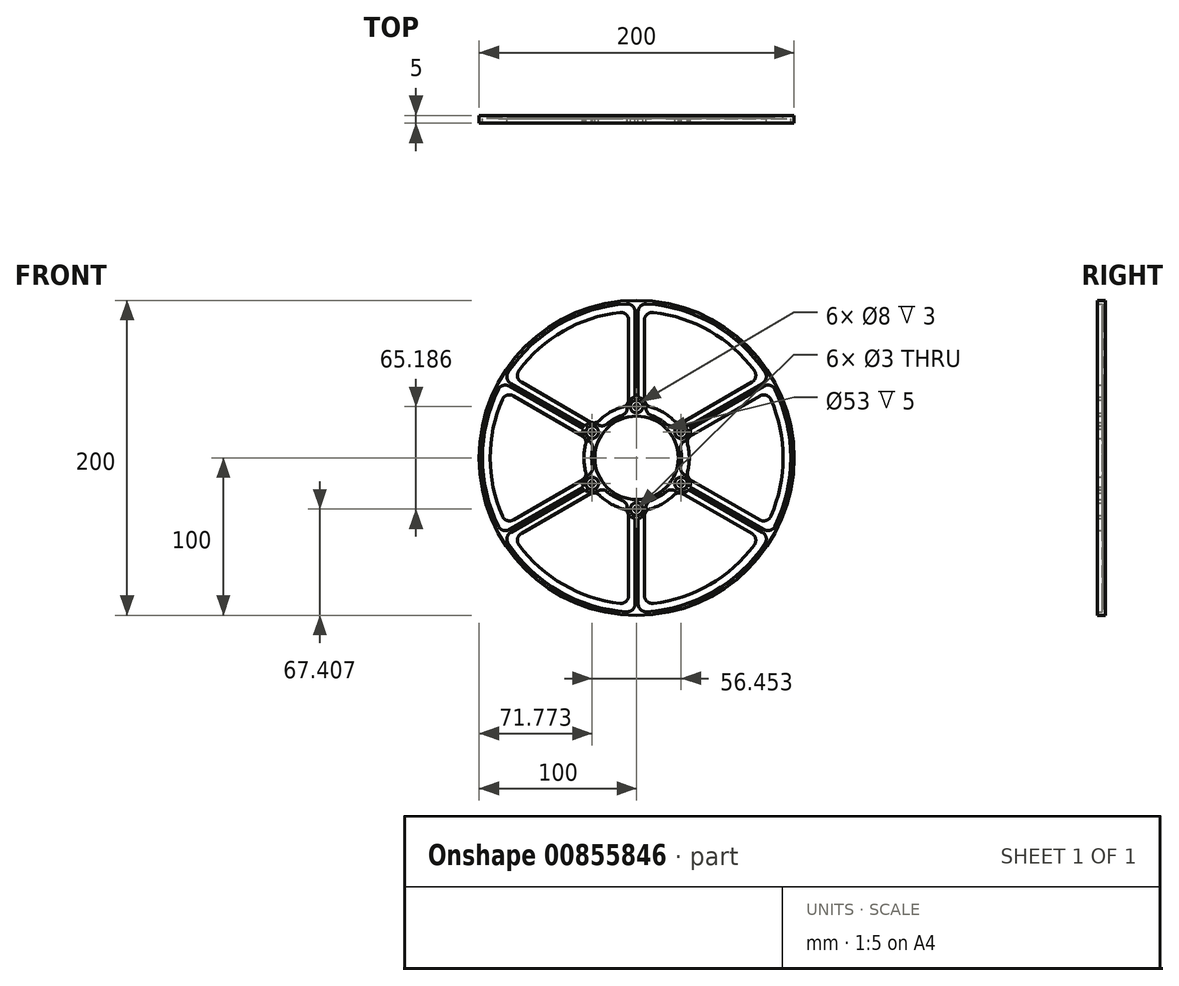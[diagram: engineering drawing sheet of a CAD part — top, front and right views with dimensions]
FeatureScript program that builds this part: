
annotation { "Feature Type Name" : "Feature", "Feature Type Description" : "" }
export const myFeature = defineFeature(function(context is Context, id is Id, definition is map)
    precondition{}
    {
        {
            var Q0;
            Q0=qCreatedBy(makeId("Front.planeOp"),FACE);
            var sketch = newSketch(context, id + "F0", { "sketchPlane" : qUnion([Q0])});
            skCircle(sketch, "E0", {"center": v(0, 0) * mm, "radius": 100 * mm});
            skCircle(sketch, "E1", {"center": v(0, 0) * mm, "radius": 93 * mm});
            skSolve(sketch);
        }
        {
            var Q0;
            Q0 = qSketchRegion(id + "F0", true);
            extrude(context, id + "F1", {"entities" : qUnion([Q0]), "depth" : 2 * mm, "offsetDistance" : 25 * mm});
        }
        {
            var Q0;
            Q0=qCreatedBy(makeId("Front.planeOp"),FACE);
            var sketch = newSketch(context, id + "F2", { "sketchPlane" : qUnion([Q0])});
            skCircle(sketch, "E2", {"center": v(0, 0) * mm, "radius": 33.5 * mm});
            skCircle(sketch, "E3", {"center": v(0, 0) * mm, "radius": 26.5 * mm});
            skSolve(sketch);
        }
        {
            var Q0;
            Q0 = qSketchRegion(id + "F2", true);
            extrude(context, id + "F3", {"entities" : qUnion([Q0]), "depth" : 2 * mm, "offsetDistance" : 25 * mm});
        }
        {
            var Q0;
            Q0=qCreatedBy(makeId("Front.planeOp"),FACE);
            var sketch = newSketch(context, id + "F4", { "sketchPlane" : qUnion([Q0])});
            skCircle(sketch, "E4", {"center": v(0, 0) * mm, "radius": 100 * mm});
            skCircle(sketch, "E5", {"center": v(0, 0) * mm, "radius": 98 * mm});
            skSolve(sketch);
        }
        {
            var Q0;
            Q0 = qSketchRegion(id + "F4", true);
            extrude(context, id + "F5", {"entities" : qUnion([Q0]), "operationType" : NewBodyOperationType.ADD, "depth" : 5 * mm, "offsetDistance" : 25 * mm});
        }
        {
            var Q0;
            Q0=qCreatedBy(makeId("Front.planeOp"),FACE);
            var sketch = newSketch(context, id + "F6", { "sketchPlane" : qUnion([Q0])});
            skCircle(sketch, "E6", {"center": v(0, 0) * mm, "radius": 26.5 * mm});
            skCircle(sketch, "E7", {"center": v(0, 0) * mm, "radius": 28.5 * mm});
            skSolve(sketch);
        }
        {
            var Q0;
            Q0 = qSketchRegion(id + "F6", true);
            extrude(context, id + "F7", {"entities" : qUnion([Q0]), "operationType" : NewBodyOperationType.ADD, "depth" : 5 * mm, "offsetDistance" : 25 * mm});
        }
        {
            var Q0;
            Q0=qCreatedBy(makeId("Front.planeOp"),FACE);
            var sketch = newSketch(context, id + "F8", { "sketchPlane" : qUnion([Q0])});
            skLineSegment(sketch, "E8.bottom", {"start": v(-5, 95.2) * mm, "end": v(5, 95.2) * mm});
            skLineSegment(sketch, "E8.top", {"start": v(-5, 31.67) * mm, "end": v(5, 31.67) * mm});
            skLineSegment(sketch, "E8.left", {"start": v(-5, 95.2) * mm, "end": v(-5, 31.67) * mm});
            skLineSegment(sketch, "E8.right", {"start": v(5, 95.2) * mm, "end": v(5, 31.67) * mm});
            skLineSegment(sketch, "E9.1.0", {"start": v(-84.95, 43.27) * mm, "end": v(-79.95, 51.93) * mm});
            skLineSegment(sketch, "E9.1.1", {"start": v(-84.95, 43.27) * mm, "end": v(-29.93, 11.5) * mm});
            skLineSegment(sketch, "E9.1.2", {"start": v(-29.93, 11.5) * mm, "end": v(-24.93, 20.16) * mm});
            skLineSegment(sketch, "E9.1.3", {"start": v(-79.95, 51.93) * mm, "end": v(-24.93, 20.16) * mm});
            skLineSegment(sketch, "E9.2.0", {"start": v(-79.95, -51.93) * mm, "end": v(-84.95, -43.27) * mm});
            skLineSegment(sketch, "E9.2.1", {"start": v(-79.95, -51.93) * mm, "end": v(-24.93, -20.16) * mm});
            skLineSegment(sketch, "E9.2.2", {"start": v(-24.93, -20.16) * mm, "end": v(-29.93, -11.5) * mm});
            skLineSegment(sketch, "E9.2.3", {"start": v(-84.95, -43.27) * mm, "end": v(-29.93, -11.5) * mm});
            skLineSegment(sketch, "E9.3.0", {"start": v(5, -95.2) * mm, "end": v(-5, -95.2) * mm});
            skLineSegment(sketch, "E9.3.1", {"start": v(5, -95.2) * mm, "end": v(5, -31.67) * mm});
            skLineSegment(sketch, "E9.3.2", {"start": v(5, -31.67) * mm, "end": v(-5, -31.67) * mm});
            skLineSegment(sketch, "E9.3.3", {"start": v(-5, -95.2) * mm, "end": v(-5, -31.67) * mm});
            skLineSegment(sketch, "E9.4.0", {"start": v(84.95, -43.27) * mm, "end": v(79.95, -51.93) * mm});
            skLineSegment(sketch, "E9.4.1", {"start": v(84.95, -43.27) * mm, "end": v(29.93, -11.5) * mm});
            skLineSegment(sketch, "E9.4.2", {"start": v(29.93, -11.5) * mm, "end": v(24.93, -20.16) * mm});
            skLineSegment(sketch, "E9.4.3", {"start": v(79.95, -51.93) * mm, "end": v(24.93, -20.16) * mm});
            skLineSegment(sketch, "E9.5.0", {"start": v(79.95, 51.93) * mm, "end": v(84.95, 43.27) * mm});
            skLineSegment(sketch, "E9.5.1", {"start": v(79.95, 51.93) * mm, "end": v(24.93, 20.16) * mm});
            skLineSegment(sketch, "E9.5.2", {"start": v(24.93, 20.16) * mm, "end": v(29.93, 11.5) * mm});
            skLineSegment(sketch, "E9.5.3", {"start": v(84.95, 43.27) * mm, "end": v(29.93, 11.5) * mm});
            skPoint(sketch, "E9.center", {"position": v(0, 0) * mm});
            skSolve(sketch);
        }
        {
            var Q0;
            Q0 = qSketchRegion(id + "F8", true);
            extrude(context, id + "F9", {"entities" : qUnion([Q0]), "depth" : 2 * mm, "offsetDistance" : 25 * mm});
        }
        {
            var Q0;
            Q0=qCreatedBy(makeId("Front.planeOp"),FACE);
            var sketch = newSketch(context, id + "F10", { "sketchPlane" : qUnion([Q0])});
            skLineSegment(sketch, "E10.bottom", {"start": v(-1, 98.62) * mm, "end": v(1, 98.62) * mm});
            skLineSegment(sketch, "E10.top", {"start": v(-1, 36.92) * mm, "end": v(1, 36.92) * mm});
            skLineSegment(sketch, "E10.left", {"start": v(-1, 98.62) * mm, "end": v(-1, 36.92) * mm});
            skLineSegment(sketch, "E10.right", {"start": v(1, 98.62) * mm, "end": v(1, 36.92) * mm});
            skLineSegment(sketch, "E11.1.0", {"start": v(-84.9, 50.17) * mm, "end": v(-31.47, 19.32) * mm});
            skLineSegment(sketch, "E11.1.1", {"start": v(-85.9, 48.44) * mm, "end": v(-32.47, 17.6) * mm});
            skLineSegment(sketch, "E11.1.2", {"start": v(-32.47, 17.6) * mm, "end": v(-31.47, 19.32) * mm});
            skLineSegment(sketch, "E11.1.3", {"start": v(-85.9, 48.44) * mm, "end": v(-84.9, 50.17) * mm});
            skLineSegment(sketch, "E11.2.0", {"start": v(-85.9, -48.44) * mm, "end": v(-32.47, -17.6) * mm});
            skLineSegment(sketch, "E11.2.1", {"start": v(-84.9, -50.17) * mm, "end": v(-31.47, -19.32) * mm});
            skLineSegment(sketch, "E11.2.2", {"start": v(-31.47, -19.32) * mm, "end": v(-32.47, -17.6) * mm});
            skLineSegment(sketch, "E11.2.3", {"start": v(-84.9, -50.17) * mm, "end": v(-85.9, -48.44) * mm});
            skLineSegment(sketch, "E11.3.0", {"start": v(-1, -98.62) * mm, "end": v(-1, -36.92) * mm});
            skLineSegment(sketch, "E11.3.1", {"start": v(1, -98.62) * mm, "end": v(1, -36.92) * mm});
            skLineSegment(sketch, "E11.3.2", {"start": v(1, -36.92) * mm, "end": v(-1, -36.92) * mm});
            skLineSegment(sketch, "E11.3.3", {"start": v(1, -98.62) * mm, "end": v(-1, -98.62) * mm});
            skLineSegment(sketch, "E11.4.0", {"start": v(84.9, -50.17) * mm, "end": v(31.47, -19.32) * mm});
            skLineSegment(sketch, "E11.4.1", {"start": v(85.9, -48.44) * mm, "end": v(32.47, -17.6) * mm});
            skLineSegment(sketch, "E11.4.2", {"start": v(32.47, -17.6) * mm, "end": v(31.47, -19.32) * mm});
            skLineSegment(sketch, "E11.4.3", {"start": v(85.9, -48.44) * mm, "end": v(84.9, -50.17) * mm});
            skLineSegment(sketch, "E11.5.0", {"start": v(85.9, 48.44) * mm, "end": v(32.47, 17.6) * mm});
            skLineSegment(sketch, "E11.5.1", {"start": v(84.9, 50.17) * mm, "end": v(31.47, 19.32) * mm});
            skLineSegment(sketch, "E11.5.2", {"start": v(31.47, 19.32) * mm, "end": v(32.47, 17.6) * mm});
            skLineSegment(sketch, "E11.5.3", {"start": v(84.9, 50.17) * mm, "end": v(85.9, 48.44) * mm});
            skPoint(sketch, "E11.center", {"position": v(0, 0) * mm});
            skSolve(sketch);
        }
        {
            var Q0;
            Q0 = qSketchRegion(id + "F10", true);
            extrude(context, id + "F11", {"entities" : qUnion([Q0]), "depth" : 5 * mm, "offsetDistance" : 25 * mm});
        }
        {
            var Q0;
            Q0=qCreatedBy(makeId("Front.planeOp"),FACE);
            var sketch = newSketch(context, id + "F12", { "sketchPlane" : qUnion([Q0])});
            skCircle(sketch, "E12", {"center": v(0, 32.6) * mm, "radius": 4 * mm});
            skCircle(sketch, "E13", {"center": v(0, 32.6) * mm, "radius": 6 * mm});
            skCircle(sketch, "E14.1.0", {"center": v(-28.23, 16.3) * mm, "radius": 4 * mm});
            skCircle(sketch, "E14.1.1", {"center": v(-28.23, 16.3) * mm, "radius": 6 * mm});
            skCircle(sketch, "E14.2.0", {"center": v(-28.23, -16.3) * mm, "radius": 4 * mm});
            skCircle(sketch, "E14.2.1", {"center": v(-28.23, -16.3) * mm, "radius": 6 * mm});
            skCircle(sketch, "E14.3.0", {"center": v(0, -32.6) * mm, "radius": 4 * mm});
            skCircle(sketch, "E14.3.1", {"center": v(0, -32.6) * mm, "radius": 6 * mm});
            skCircle(sketch, "E14.4.0", {"center": v(28.23, -16.3) * mm, "radius": 4 * mm});
            skCircle(sketch, "E14.4.1", {"center": v(28.23, -16.3) * mm, "radius": 6 * mm});
            skCircle(sketch, "E14.5.0", {"center": v(28.23, 16.3) * mm, "radius": 4 * mm});
            skCircle(sketch, "E14.5.1", {"center": v(28.23, 16.3) * mm, "radius": 6 * mm});
            skPoint(sketch, "E14.center", {"position": v(0, 0) * mm});
            skSolve(sketch);
        }
        {
            var Q0;
            Q0 = qSketchRegion(id + "F12", true);
            extrude(context, id + "F13", {"entities" : qUnion([Q0]), "operationType" : NewBodyOperationType.ADD, "depth" : 5 * mm, "offsetDistance" : 25 * mm});
        }
        {
            var Q0;
            Q0=makeQuery(id+"F3.opExtrude","SWEPT_BODY",BODY,{"disambiguationData":[OSD([sQuery(id+"F2.wireOp",EDGE,"E2"),sQuery(id+"F2.wireOp",EDGE,"E3")])]});
            var Q1;
            Q1=makeQuery(id+"F9.opExtrude","SWEPT_BODY",BODY,{"disambiguationData":[OSD([sQuery(id+"F8.wireOp",EDGE,"E8.bottom"),sQuery(id+"F8.wireOp",EDGE,"E8.top"),sQuery(id+"F8.wireOp",EDGE,"E8.left"),sQuery(id+"F8.wireOp",EDGE,"E8.right")])]});
            var Q2;
            Q2=makeQuery(id+"F11.opExtrude","SWEPT_BODY",BODY,{"disambiguationData":[OSD([sQuery(id+"F10.wireOp",EDGE,"E10.bottom"),sQuery(id+"F10.wireOp",EDGE,"E10.top"),sQuery(id+"F10.wireOp",EDGE,"E10.left"),sQuery(id+"F10.wireOp",EDGE,"E10.right")])]});
            var Q3;
            Q3=makeQuery(id+"F1.opExtrude","SWEPT_BODY",BODY,{"disambiguationData":[OSD([sQuery(id+"F0.wireOp",EDGE,"E0"),sQuery(id+"F0.wireOp",EDGE,"E1")])]});
            var Q4;
            Q4=makeQuery(id+"F9.opExtrude","SWEPT_BODY",BODY,{"disambiguationData":[OSD([sQuery(id+"F8.wireOp",EDGE,"E9.5.0"),sQuery(id+"F8.wireOp",EDGE,"E9.5.1"),sQuery(id+"F8.wireOp",EDGE,"E9.5.2"),sQuery(id+"F8.wireOp",EDGE,"E9.5.3")])]});
            var Q5;
            Q5=makeQuery(id+"F11.opExtrude","SWEPT_BODY",BODY,{"disambiguationData":[OSD([sQuery(id+"F10.wireOp",EDGE,"E11.5.0"),sQuery(id+"F10.wireOp",EDGE,"E11.5.1"),sQuery(id+"F10.wireOp",EDGE,"E11.5.2"),sQuery(id+"F10.wireOp",EDGE,"E11.5.3")])]});
            var Q6;
            Q6=makeQuery(id+"F9.opExtrude","SWEPT_BODY",BODY,{"disambiguationData":[OSD([sQuery(id+"F8.wireOp",EDGE,"E9.4.0"),sQuery(id+"F8.wireOp",EDGE,"E9.4.1"),sQuery(id+"F8.wireOp",EDGE,"E9.4.2"),sQuery(id+"F8.wireOp",EDGE,"E9.4.3")])]});
            var Q7;
            Q7=makeQuery(id+"F11.opExtrude","SWEPT_BODY",BODY,{"disambiguationData":[OSD([sQuery(id+"F10.wireOp",EDGE,"E11.4.0"),sQuery(id+"F10.wireOp",EDGE,"E11.4.1"),sQuery(id+"F10.wireOp",EDGE,"E11.4.2"),sQuery(id+"F10.wireOp",EDGE,"E11.4.3")])]});
            var Q8;
            Q8=makeQuery(id+"F9.opExtrude","SWEPT_BODY",BODY,{"disambiguationData":[OSD([sQuery(id+"F8.wireOp",EDGE,"E9.3.0"),sQuery(id+"F8.wireOp",EDGE,"E9.3.1"),sQuery(id+"F8.wireOp",EDGE,"E9.3.2"),sQuery(id+"F8.wireOp",EDGE,"E9.3.3")])]});
            var Q9;
            Q9=makeQuery(id+"F11.opExtrude","SWEPT_BODY",BODY,{"disambiguationData":[OSD([sQuery(id+"F10.wireOp",EDGE,"E11.3.0"),sQuery(id+"F10.wireOp",EDGE,"E11.3.1"),sQuery(id+"F10.wireOp",EDGE,"E11.3.2"),sQuery(id+"F10.wireOp",EDGE,"E11.3.3")])]});
            var Q10;
            Q10=makeQuery(id+"F11.opExtrude","SWEPT_BODY",BODY,{"disambiguationData":[OSD([sQuery(id+"F10.wireOp",EDGE,"E11.2.0"),sQuery(id+"F10.wireOp",EDGE,"E11.2.1"),sQuery(id+"F10.wireOp",EDGE,"E11.2.2"),sQuery(id+"F10.wireOp",EDGE,"E11.2.3")])]});
            var Q11;
            Q11=makeQuery(id+"F9.opExtrude","SWEPT_BODY",BODY,{"disambiguationData":[OSD([sQuery(id+"F8.wireOp",EDGE,"E9.2.0"),sQuery(id+"F8.wireOp",EDGE,"E9.2.1"),sQuery(id+"F8.wireOp",EDGE,"E9.2.2"),sQuery(id+"F8.wireOp",EDGE,"E9.2.3")])]});
            var Q12;
            Q12=makeQuery(id+"F9.opExtrude","SWEPT_BODY",BODY,{"disambiguationData":[OSD([sQuery(id+"F8.wireOp",EDGE,"E9.1.0"),sQuery(id+"F8.wireOp",EDGE,"E9.1.1"),sQuery(id+"F8.wireOp",EDGE,"E9.1.2"),sQuery(id+"F8.wireOp",EDGE,"E9.1.3")])]});
            var Q13;
            Q13=makeQuery(id+"F11.opExtrude","SWEPT_BODY",BODY,{"disambiguationData":[OSD([sQuery(id+"F10.wireOp",EDGE,"E11.1.0"),sQuery(id+"F10.wireOp",EDGE,"E11.1.1"),sQuery(id+"F10.wireOp",EDGE,"E11.1.2"),sQuery(id+"F10.wireOp",EDGE,"E11.1.3")])]});
            booleanBodies(context, id + "F14", {"operationType" : BooleanOperationType.UNION, "tools" : qUnion([Q0, Q1, Q2, Q3, Q4, Q5, Q6, Q7, Q8, Q9, Q10, Q11, Q12, Q13])});
        }
        {
            var Q0;
            Q0=qCreatedBy(makeId("Front.planeOp"),FACE);
            var sketch = newSketch(context, id + "F15", { "sketchPlane" : qUnion([Q0])});
            skCircle(sketch, "E15", {"center": v(0, 32.6) * mm, "radius": 1.5 * mm});
            skCircle(sketch, "E16.1.0", {"center": v(-28.23, 16.3) * mm, "radius": 1.5 * mm});
            skCircle(sketch, "E16.2.0", {"center": v(-28.23, -16.3) * mm, "radius": 1.5 * mm});
            skCircle(sketch, "E16.3.0", {"center": v(0, -32.6) * mm, "radius": 1.5 * mm});
            skCircle(sketch, "E16.4.0", {"center": v(28.23, -16.3) * mm, "radius": 1.5 * mm});
            skCircle(sketch, "E16.5.0", {"center": v(28.23, 16.3) * mm, "radius": 1.5 * mm});
            skPoint(sketch, "E16.center", {"position": v(0, 0) * mm});
            skSolve(sketch);
        }
        {
            var Q0;
            Q0 = qSketchRegion(id + "F15", true);
            extrude(context, id + "F16", {"entities" : qUnion([Q0]), "operationType" : NewBodyOperationType.REMOVE, "endBound" : BoundingType.THROUGH_ALL, "depth" : 5 * mm, "offsetDistance" : 25 * mm});
        }
        {
            var Q0;
            Q0=makeQuery(id+"F14.opBoolean","INTERSECT",EDGE,{"derivedFrom":[makeQuery(id+"F11.opExtrude","SWEPT_FACE",FACE,{"disambiguationData":[OSD([sQuery(id+"F10.wireOp",EDGE,"E10.right")])]}),makeQuery(id+"F13.opExtrude","SWEPT_FACE",FACE,{"disambiguationData":[OSD([sQuery(id+"F12.wireOp",EDGE,"E13")])]})]});
            var Q1;
            Q1=makeQuery(id+"F13.boolean.opBoolean","INTERSECT",EDGE,{"disambiguationData":[OD(1.0)],"derivedFrom":[makeQuery(id+"F7.opExtrude","SWEPT_FACE",FACE,{"disambiguationData":[OSD([sQuery(id+"F6.wireOp",EDGE,"E7")])]}),makeQuery(id+"F13.opExtrude","SWEPT_FACE",FACE,{"disambiguationData":[OSD([sQuery(id+"F12.wireOp",EDGE,"E13")])]})]});
            var Q2;
            Q2=makeQuery(id+"F13.boolean.opBoolean","INTERSECT",EDGE,{"disambiguationData":[OD(1.0)],"derivedFrom":[makeQuery(id+"F3.opExtrude","SWEPT_FACE",FACE,{"disambiguationData":[OSD([sQuery(id+"F2.wireOp",EDGE,"E2")])]}),makeQuery(id+"F13.opExtrude","SWEPT_FACE",FACE,{"disambiguationData":[OSD([sQuery(id+"F12.wireOp",EDGE,"E13")])]})]});
            var Q3;
            Q3=makeQuery(id+"F13.boolean.opBoolean","INTERSECT",EDGE,{"disambiguationData":[OD(0.0)],"derivedFrom":[makeQuery(id+"F7.opExtrude","SWEPT_FACE",FACE,{"disambiguationData":[OSD([sQuery(id+"F6.wireOp",EDGE,"E7")])]}),makeQuery(id+"F13.opExtrude","SWEPT_FACE",FACE,{"disambiguationData":[OSD([sQuery(id+"F12.wireOp",EDGE,"E13")])]})]});
            var Q4;
            Q4=makeQuery(id+"F14.opBoolean","INTERSECT",EDGE,{"derivedFrom":[makeQuery(id+"F11.opExtrude","SWEPT_FACE",FACE,{"disambiguationData":[OSD([sQuery(id+"F10.wireOp",EDGE,"E10.left")])]}),makeQuery(id+"F13.opExtrude","SWEPT_FACE",FACE,{"disambiguationData":[OSD([sQuery(id+"F12.wireOp",EDGE,"E13")])]})]});
            var Q5;
            Q5=makeQuery(id+"F13.boolean.opBoolean","INTERSECT",EDGE,{"disambiguationData":[OD(0.0)],"derivedFrom":[makeQuery(id+"F3.opExtrude","SWEPT_FACE",FACE,{"disambiguationData":[OSD([sQuery(id+"F2.wireOp",EDGE,"E2")])]}),makeQuery(id+"F13.opExtrude","SWEPT_FACE",FACE,{"disambiguationData":[OSD([sQuery(id+"F12.wireOp",EDGE,"E13")])]})]});
            var Q6;
            Q6=makeQuery(id+"F14.opBoolean","INTERSECT",EDGE,{"derivedFrom":[makeQuery(id+"F5.opExtrude","SWEPT_FACE",FACE,{"disambiguationData":[OSD([sQuery(id+"F4.wireOp",EDGE,"E5")])]}),makeQuery(id+"F11.opExtrude","SWEPT_FACE",FACE,{"disambiguationData":[OSD([sQuery(id+"F10.wireOp",EDGE,"E10.right")])]})]});
            var Q7;
            Q7=makeQuery(id+"F14.opBoolean","INTERSECT",EDGE,{"derivedFrom":[makeQuery(id+"F5.opExtrude","SWEPT_FACE",FACE,{"disambiguationData":[OSD([sQuery(id+"F4.wireOp",EDGE,"E5")])]}),makeQuery(id+"F11.opExtrude","SWEPT_FACE",FACE,{"disambiguationData":[OSD([sQuery(id+"F10.wireOp",EDGE,"E10.left")])]})]});
            var Q8;
            Q8=makeQuery(id+"F13.boolean.opBoolean","INTERSECT",EDGE,{"disambiguationData":[OD(1.0)],"derivedFrom":[makeQuery(id+"F3.opExtrude","SWEPT_FACE",FACE,{"disambiguationData":[OSD([sQuery(id+"F2.wireOp",EDGE,"E2")])]}),makeQuery(id+"F13.opExtrude","SWEPT_FACE",FACE,{"disambiguationData":[OSD([sQuery(id+"F12.wireOp",EDGE,"E14.5.1")])]})]});
            var Q9;
            Q9=makeQuery(id+"F13.boolean.opBoolean","INTERSECT",EDGE,{"disambiguationData":[OD(1.0)],"derivedFrom":[makeQuery(id+"F7.opExtrude","SWEPT_FACE",FACE,{"disambiguationData":[OSD([sQuery(id+"F6.wireOp",EDGE,"E7")])]}),makeQuery(id+"F13.opExtrude","SWEPT_FACE",FACE,{"disambiguationData":[OSD([sQuery(id+"F12.wireOp",EDGE,"E14.5.1")])]})]});
            var Q10;
            Q10=makeQuery(id+"F14.opBoolean","INTERSECT",EDGE,{"derivedFrom":[makeQuery(id+"F11.opExtrude","SWEPT_FACE",FACE,{"disambiguationData":[OSD([sQuery(id+"F10.wireOp",EDGE,"E11.5.0")])]}),makeQuery(id+"F13.opExtrude","SWEPT_FACE",FACE,{"disambiguationData":[OSD([sQuery(id+"F12.wireOp",EDGE,"E14.5.1")])]})]});
            var Q11;
            Q11=makeQuery(id+"F13.boolean.opBoolean","INTERSECT",EDGE,{"disambiguationData":[OD(0.0)],"derivedFrom":[makeQuery(id+"F7.opExtrude","SWEPT_FACE",FACE,{"disambiguationData":[OSD([sQuery(id+"F6.wireOp",EDGE,"E7")])]}),makeQuery(id+"F13.opExtrude","SWEPT_FACE",FACE,{"disambiguationData":[OSD([sQuery(id+"F12.wireOp",EDGE,"E14.5.1")])]})]});
            var Q12;
            Q12=makeQuery(id+"F14.opBoolean","INTERSECT",EDGE,{"derivedFrom":[makeQuery(id+"F11.opExtrude","SWEPT_FACE",FACE,{"disambiguationData":[OSD([sQuery(id+"F10.wireOp",EDGE,"E11.5.1")])]}),makeQuery(id+"F13.opExtrude","SWEPT_FACE",FACE,{"disambiguationData":[OSD([sQuery(id+"F12.wireOp",EDGE,"E14.5.1")])]})]});
            var Q13;
            Q13=makeQuery(id+"F13.boolean.opBoolean","INTERSECT",EDGE,{"disambiguationData":[OD(0.0)],"derivedFrom":[makeQuery(id+"F3.opExtrude","SWEPT_FACE",FACE,{"disambiguationData":[OSD([sQuery(id+"F2.wireOp",EDGE,"E2")])]}),makeQuery(id+"F13.opExtrude","SWEPT_FACE",FACE,{"disambiguationData":[OSD([sQuery(id+"F12.wireOp",EDGE,"E14.5.1")])]})]});
            var Q14;
            Q14=makeQuery(id+"F13.boolean.opBoolean","INTERSECT",EDGE,{"disambiguationData":[OD(1.0)],"derivedFrom":[makeQuery(id+"F7.opExtrude","SWEPT_FACE",FACE,{"disambiguationData":[OSD([sQuery(id+"F6.wireOp",EDGE,"E7")])]}),makeQuery(id+"F13.opExtrude","SWEPT_FACE",FACE,{"disambiguationData":[OSD([sQuery(id+"F12.wireOp",EDGE,"E14.4.1")])]})]});
            var Q15;
            Q15=makeQuery(id+"F14.opBoolean","INTERSECT",EDGE,{"derivedFrom":[makeQuery(id+"F11.opExtrude","SWEPT_FACE",FACE,{"disambiguationData":[OSD([sQuery(id+"F10.wireOp",EDGE,"E11.4.1")])]}),makeQuery(id+"F13.opExtrude","SWEPT_FACE",FACE,{"disambiguationData":[OSD([sQuery(id+"F12.wireOp",EDGE,"E14.4.1")])]})]});
            var Q16;
            Q16=makeQuery(id+"F13.boolean.opBoolean","INTERSECT",EDGE,{"disambiguationData":[OD(1.0)],"derivedFrom":[makeQuery(id+"F3.opExtrude","SWEPT_FACE",FACE,{"disambiguationData":[OSD([sQuery(id+"F2.wireOp",EDGE,"E2")])]}),makeQuery(id+"F13.opExtrude","SWEPT_FACE",FACE,{"disambiguationData":[OSD([sQuery(id+"F12.wireOp",EDGE,"E14.4.1")])]})]});
            var Q17;
            Q17=makeQuery(id+"F14.opBoolean","INTERSECT",EDGE,{"derivedFrom":[makeQuery(id+"F11.opExtrude","SWEPT_FACE",FACE,{"disambiguationData":[OSD([sQuery(id+"F10.wireOp",EDGE,"E11.4.0")])]}),makeQuery(id+"F13.opExtrude","SWEPT_FACE",FACE,{"disambiguationData":[OSD([sQuery(id+"F12.wireOp",EDGE,"E14.4.1")])]})]});
            var Q18;
            Q18=makeQuery(id+"F13.boolean.opBoolean","INTERSECT",EDGE,{"disambiguationData":[OD(0.0)],"derivedFrom":[makeQuery(id+"F7.opExtrude","SWEPT_FACE",FACE,{"disambiguationData":[OSD([sQuery(id+"F6.wireOp",EDGE,"E7")])]}),makeQuery(id+"F13.opExtrude","SWEPT_FACE",FACE,{"disambiguationData":[OSD([sQuery(id+"F12.wireOp",EDGE,"E14.4.1")])]})]});
            var Q19;
            Q19=makeQuery(id+"F13.boolean.opBoolean","INTERSECT",EDGE,{"disambiguationData":[OD(0.0)],"derivedFrom":[makeQuery(id+"F3.opExtrude","SWEPT_FACE",FACE,{"disambiguationData":[OSD([sQuery(id+"F2.wireOp",EDGE,"E2")])]}),makeQuery(id+"F13.opExtrude","SWEPT_FACE",FACE,{"disambiguationData":[OSD([sQuery(id+"F12.wireOp",EDGE,"E14.4.1")])]})]});
            var Q20;
            Q20=makeQuery(id+"F13.boolean.opBoolean","INTERSECT",EDGE,{"disambiguationData":[OD(1.0)],"derivedFrom":[makeQuery(id+"F7.opExtrude","SWEPT_FACE",FACE,{"disambiguationData":[OSD([sQuery(id+"F6.wireOp",EDGE,"E7")])]}),makeQuery(id+"F13.opExtrude","SWEPT_FACE",FACE,{"disambiguationData":[OSD([sQuery(id+"F12.wireOp",EDGE,"E14.3.1")])]})]});
            var Q21;
            Q21=makeQuery(id+"F13.boolean.opBoolean","INTERSECT",EDGE,{"disambiguationData":[OD(1.0)],"derivedFrom":[makeQuery(id+"F3.opExtrude","SWEPT_FACE",FACE,{"disambiguationData":[OSD([sQuery(id+"F2.wireOp",EDGE,"E2")])]}),makeQuery(id+"F13.opExtrude","SWEPT_FACE",FACE,{"disambiguationData":[OSD([sQuery(id+"F12.wireOp",EDGE,"E14.3.1")])]})]});
            var Q22;
            Q22=makeQuery(id+"F14.opBoolean","INTERSECT",EDGE,{"derivedFrom":[makeQuery(id+"F11.opExtrude","SWEPT_FACE",FACE,{"disambiguationData":[OSD([sQuery(id+"F10.wireOp",EDGE,"E11.3.1")])]}),makeQuery(id+"F13.opExtrude","SWEPT_FACE",FACE,{"disambiguationData":[OSD([sQuery(id+"F12.wireOp",EDGE,"E14.3.1")])]})]});
            var Q23;
            Q23=makeQuery(id+"F13.boolean.opBoolean","INTERSECT",EDGE,{"disambiguationData":[OD(0.0)],"derivedFrom":[makeQuery(id+"F7.opExtrude","SWEPT_FACE",FACE,{"disambiguationData":[OSD([sQuery(id+"F6.wireOp",EDGE,"E7")])]}),makeQuery(id+"F13.opExtrude","SWEPT_FACE",FACE,{"disambiguationData":[OSD([sQuery(id+"F12.wireOp",EDGE,"E14.3.1")])]})]});
            var Q24;
            Q24=makeQuery(id+"F14.opBoolean","INTERSECT",EDGE,{"derivedFrom":[makeQuery(id+"F11.opExtrude","SWEPT_FACE",FACE,{"disambiguationData":[OSD([sQuery(id+"F10.wireOp",EDGE,"E11.3.0")])]}),makeQuery(id+"F13.opExtrude","SWEPT_FACE",FACE,{"disambiguationData":[OSD([sQuery(id+"F12.wireOp",EDGE,"E14.3.1")])]})]});
            var Q25;
            Q25=makeQuery(id+"F13.boolean.opBoolean","INTERSECT",EDGE,{"disambiguationData":[OD(0.0)],"derivedFrom":[makeQuery(id+"F3.opExtrude","SWEPT_FACE",FACE,{"disambiguationData":[OSD([sQuery(id+"F2.wireOp",EDGE,"E2")])]}),makeQuery(id+"F13.opExtrude","SWEPT_FACE",FACE,{"disambiguationData":[OSD([sQuery(id+"F12.wireOp",EDGE,"E14.3.1")])]})]});
            var Q26;
            Q26=makeQuery(id+"F13.boolean.opBoolean","INTERSECT",EDGE,{"disambiguationData":[OD(1.0)],"derivedFrom":[makeQuery(id+"F7.opExtrude","SWEPT_FACE",FACE,{"disambiguationData":[OSD([sQuery(id+"F6.wireOp",EDGE,"E7")])]}),makeQuery(id+"F13.opExtrude","SWEPT_FACE",FACE,{"disambiguationData":[OSD([sQuery(id+"F12.wireOp",EDGE,"E14.2.1")])]})]});
            var Q27;
            Q27=makeQuery(id+"F13.boolean.opBoolean","INTERSECT",EDGE,{"disambiguationData":[OD(1.0)],"derivedFrom":[makeQuery(id+"F3.opExtrude","SWEPT_FACE",FACE,{"disambiguationData":[OSD([sQuery(id+"F2.wireOp",EDGE,"E2")])]}),makeQuery(id+"F13.opExtrude","SWEPT_FACE",FACE,{"disambiguationData":[OSD([sQuery(id+"F12.wireOp",EDGE,"E14.2.1")])]})]});
            var Q28;
            Q28=makeQuery(id+"F14.opBoolean","INTERSECT",EDGE,{"derivedFrom":[makeQuery(id+"F11.opExtrude","SWEPT_FACE",FACE,{"disambiguationData":[OSD([sQuery(id+"F10.wireOp",EDGE,"E11.2.1")])]}),makeQuery(id+"F13.opExtrude","SWEPT_FACE",FACE,{"disambiguationData":[OSD([sQuery(id+"F12.wireOp",EDGE,"E14.2.1")])]})]});
            var Q29;
            Q29=makeQuery(id+"F13.boolean.opBoolean","INTERSECT",EDGE,{"disambiguationData":[OD(0.0)],"derivedFrom":[makeQuery(id+"F7.opExtrude","SWEPT_FACE",FACE,{"disambiguationData":[OSD([sQuery(id+"F6.wireOp",EDGE,"E7")])]}),makeQuery(id+"F13.opExtrude","SWEPT_FACE",FACE,{"disambiguationData":[OSD([sQuery(id+"F12.wireOp",EDGE,"E14.2.1")])]})]});
            var Q30;
            Q30=makeQuery(id+"F14.opBoolean","INTERSECT",EDGE,{"derivedFrom":[makeQuery(id+"F11.opExtrude","SWEPT_FACE",FACE,{"disambiguationData":[OSD([sQuery(id+"F10.wireOp",EDGE,"E11.2.0")])]}),makeQuery(id+"F13.opExtrude","SWEPT_FACE",FACE,{"disambiguationData":[OSD([sQuery(id+"F12.wireOp",EDGE,"E14.2.1")])]})]});
            var Q31;
            Q31=makeQuery(id+"F13.boolean.opBoolean","INTERSECT",EDGE,{"disambiguationData":[OD(0.0)],"derivedFrom":[makeQuery(id+"F3.opExtrude","SWEPT_FACE",FACE,{"disambiguationData":[OSD([sQuery(id+"F2.wireOp",EDGE,"E2")])]}),makeQuery(id+"F13.opExtrude","SWEPT_FACE",FACE,{"disambiguationData":[OSD([sQuery(id+"F12.wireOp",EDGE,"E14.2.1")])]})]});
            var Q32;
            Q32=makeQuery(id+"F13.boolean.opBoolean","INTERSECT",EDGE,{"disambiguationData":[OD(1.0)],"derivedFrom":[makeQuery(id+"F7.opExtrude","SWEPT_FACE",FACE,{"disambiguationData":[OSD([sQuery(id+"F6.wireOp",EDGE,"E7")])]}),makeQuery(id+"F13.opExtrude","SWEPT_FACE",FACE,{"disambiguationData":[OSD([sQuery(id+"F12.wireOp",EDGE,"E14.1.1")])]})]});
            var Q33;
            Q33=makeQuery(id+"F13.boolean.opBoolean","INTERSECT",EDGE,{"disambiguationData":[OD(1.0)],"derivedFrom":[makeQuery(id+"F3.opExtrude","SWEPT_FACE",FACE,{"disambiguationData":[OSD([sQuery(id+"F2.wireOp",EDGE,"E2")])]}),makeQuery(id+"F13.opExtrude","SWEPT_FACE",FACE,{"disambiguationData":[OSD([sQuery(id+"F12.wireOp",EDGE,"E14.1.1")])]})]});
            var Q34;
            Q34=makeQuery(id+"F14.opBoolean","INTERSECT",EDGE,{"derivedFrom":[makeQuery(id+"F11.opExtrude","SWEPT_FACE",FACE,{"disambiguationData":[OSD([sQuery(id+"F10.wireOp",EDGE,"E11.1.1")])]}),makeQuery(id+"F13.opExtrude","SWEPT_FACE",FACE,{"disambiguationData":[OSD([sQuery(id+"F12.wireOp",EDGE,"E14.1.1")])]})]});
            var Q35;
            Q35=makeQuery(id+"F13.boolean.opBoolean","INTERSECT",EDGE,{"disambiguationData":[OD(0.0)],"derivedFrom":[makeQuery(id+"F7.opExtrude","SWEPT_FACE",FACE,{"disambiguationData":[OSD([sQuery(id+"F6.wireOp",EDGE,"E7")])]}),makeQuery(id+"F13.opExtrude","SWEPT_FACE",FACE,{"disambiguationData":[OSD([sQuery(id+"F12.wireOp",EDGE,"E14.1.1")])]})]});
            var Q36;
            Q36=makeQuery(id+"F14.opBoolean","INTERSECT",EDGE,{"derivedFrom":[makeQuery(id+"F11.opExtrude","SWEPT_FACE",FACE,{"disambiguationData":[OSD([sQuery(id+"F10.wireOp",EDGE,"E11.1.0")])]}),makeQuery(id+"F13.opExtrude","SWEPT_FACE",FACE,{"disambiguationData":[OSD([sQuery(id+"F12.wireOp",EDGE,"E14.1.1")])]})]});
            var Q37;
            Q37=makeQuery(id+"F13.boolean.opBoolean","INTERSECT",EDGE,{"disambiguationData":[OD(0.0)],"derivedFrom":[makeQuery(id+"F3.opExtrude","SWEPT_FACE",FACE,{"disambiguationData":[OSD([sQuery(id+"F2.wireOp",EDGE,"E2")])]}),makeQuery(id+"F13.opExtrude","SWEPT_FACE",FACE,{"disambiguationData":[OSD([sQuery(id+"F12.wireOp",EDGE,"E14.1.1")])]})]});
            var Q38;
            Q38=makeQuery(id+"F14.opBoolean","INTERSECT",EDGE,{"derivedFrom":[makeQuery(id+"F5.opExtrude","SWEPT_FACE",FACE,{"disambiguationData":[OSD([sQuery(id+"F4.wireOp",EDGE,"E5")])]}),makeQuery(id+"F11.opExtrude","SWEPT_FACE",FACE,{"disambiguationData":[OSD([sQuery(id+"F10.wireOp",EDGE,"E11.3.0")])]})]});
            var Q39;
            Q39=makeQuery(id+"F14.opBoolean","INTERSECT",EDGE,{"derivedFrom":[makeQuery(id+"F1.opExtrude","SWEPT_FACE",FACE,{"disambiguationData":[OSD([sQuery(id+"F0.wireOp",EDGE,"E1")])]}),makeQuery(id+"F9.opExtrude","SWEPT_FACE",FACE,{"disambiguationData":[OSD([sQuery(id+"F8.wireOp",EDGE,"E9.3.3")])]})]});
            var Q40;
            Q40=makeQuery(id+"F14.opBoolean","INTERSECT",EDGE,{"derivedFrom":[makeQuery(id+"F5.opExtrude","SWEPT_FACE",FACE,{"disambiguationData":[OSD([sQuery(id+"F4.wireOp",EDGE,"E5")])]}),makeQuery(id+"F11.opExtrude","SWEPT_FACE",FACE,{"disambiguationData":[OSD([sQuery(id+"F10.wireOp",EDGE,"E11.3.1")])]})]});
            var Q41;
            Q41=makeQuery(id+"F14.opBoolean","INTERSECT",EDGE,{"derivedFrom":[makeQuery(id+"F1.opExtrude","SWEPT_FACE",FACE,{"disambiguationData":[OSD([sQuery(id+"F0.wireOp",EDGE,"E1")])]}),makeQuery(id+"F9.opExtrude","SWEPT_FACE",FACE,{"disambiguationData":[OSD([sQuery(id+"F8.wireOp",EDGE,"E9.3.1")])]})]});
            var Q42;
            Q42=makeQuery(id+"F14.opBoolean","INTERSECT",EDGE,{"derivedFrom":[makeQuery(id+"F5.opExtrude","SWEPT_FACE",FACE,{"disambiguationData":[OSD([sQuery(id+"F4.wireOp",EDGE,"E5")])]}),makeQuery(id+"F11.opExtrude","SWEPT_FACE",FACE,{"disambiguationData":[OSD([sQuery(id+"F10.wireOp",EDGE,"E11.4.0")])]})]});
            var Q43;
            Q43=makeQuery(id+"F14.opBoolean","INTERSECT",EDGE,{"derivedFrom":[makeQuery(id+"F1.opExtrude","SWEPT_FACE",FACE,{"disambiguationData":[OSD([sQuery(id+"F0.wireOp",EDGE,"E1")])]}),makeQuery(id+"F9.opExtrude","SWEPT_FACE",FACE,{"disambiguationData":[OSD([sQuery(id+"F8.wireOp",EDGE,"E9.4.3")])]})]});
            var Q44;
            Q44=makeQuery(id+"F14.opBoolean","INTERSECT",EDGE,{"derivedFrom":[makeQuery(id+"F5.opExtrude","SWEPT_FACE",FACE,{"disambiguationData":[OSD([sQuery(id+"F4.wireOp",EDGE,"E5")])]}),makeQuery(id+"F11.opExtrude","SWEPT_FACE",FACE,{"disambiguationData":[OSD([sQuery(id+"F10.wireOp",EDGE,"E11.4.1")])]})]});
            var Q45;
            Q45=makeQuery(id+"F14.opBoolean","INTERSECT",EDGE,{"derivedFrom":[makeQuery(id+"F1.opExtrude","SWEPT_FACE",FACE,{"disambiguationData":[OSD([sQuery(id+"F0.wireOp",EDGE,"E1")])]}),makeQuery(id+"F9.opExtrude","SWEPT_FACE",FACE,{"disambiguationData":[OSD([sQuery(id+"F8.wireOp",EDGE,"E9.4.1")])]})]});
            var Q46;
            Q46=makeQuery(id+"F14.opBoolean","INTERSECT",EDGE,{"derivedFrom":[makeQuery(id+"F5.opExtrude","SWEPT_FACE",FACE,{"disambiguationData":[OSD([sQuery(id+"F4.wireOp",EDGE,"E5")])]}),makeQuery(id+"F11.opExtrude","SWEPT_FACE",FACE,{"disambiguationData":[OSD([sQuery(id+"F10.wireOp",EDGE,"E11.5.0")])]})]});
            var Q47;
            Q47=makeQuery(id+"F14.opBoolean","INTERSECT",EDGE,{"derivedFrom":[makeQuery(id+"F1.opExtrude","SWEPT_FACE",FACE,{"disambiguationData":[OSD([sQuery(id+"F0.wireOp",EDGE,"E1")])]}),makeQuery(id+"F9.opExtrude","SWEPT_FACE",FACE,{"disambiguationData":[OSD([sQuery(id+"F8.wireOp",EDGE,"E9.5.3")])]})]});
            var Q48;
            Q48=makeQuery(id+"F14.opBoolean","INTERSECT",EDGE,{"derivedFrom":[makeQuery(id+"F5.opExtrude","SWEPT_FACE",FACE,{"disambiguationData":[OSD([sQuery(id+"F4.wireOp",EDGE,"E5")])]}),makeQuery(id+"F11.opExtrude","SWEPT_FACE",FACE,{"disambiguationData":[OSD([sQuery(id+"F10.wireOp",EDGE,"E11.5.1")])]})]});
            var Q49;
            Q49=makeQuery(id+"F14.opBoolean","INTERSECT",EDGE,{"derivedFrom":[makeQuery(id+"F1.opExtrude","SWEPT_FACE",FACE,{"disambiguationData":[OSD([sQuery(id+"F0.wireOp",EDGE,"E1")])]}),makeQuery(id+"F9.opExtrude","SWEPT_FACE",FACE,{"disambiguationData":[OSD([sQuery(id+"F8.wireOp",EDGE,"E9.5.1")])]})]});
            var Q50;
            Q50=makeQuery(id+"F14.opBoolean","INTERSECT",EDGE,{"derivedFrom":[makeQuery(id+"F1.opExtrude","SWEPT_FACE",FACE,{"disambiguationData":[OSD([sQuery(id+"F0.wireOp",EDGE,"E1")])]}),makeQuery(id+"F9.opExtrude","SWEPT_FACE",FACE,{"disambiguationData":[OSD([sQuery(id+"F8.wireOp",EDGE,"E8.right")])]})]});
            var Q51;
            Q51=makeQuery(id+"F14.opBoolean","INTERSECT",EDGE,{"derivedFrom":[makeQuery(id+"F1.opExtrude","SWEPT_FACE",FACE,{"disambiguationData":[OSD([sQuery(id+"F0.wireOp",EDGE,"E1")])]}),makeQuery(id+"F9.opExtrude","SWEPT_FACE",FACE,{"disambiguationData":[OSD([sQuery(id+"F8.wireOp",EDGE,"E8.left")])]})]});
            var Q52;
            Q52=makeQuery(id+"F14.opBoolean","INTERSECT",EDGE,{"derivedFrom":[makeQuery(id+"F1.opExtrude","SWEPT_FACE",FACE,{"disambiguationData":[OSD([sQuery(id+"F0.wireOp",EDGE,"E1")])]}),makeQuery(id+"F9.opExtrude","SWEPT_FACE",FACE,{"disambiguationData":[OSD([sQuery(id+"F8.wireOp",EDGE,"E9.1.3")])]})]});
            var Q53;
            Q53=makeQuery(id+"F14.opBoolean","INTERSECT",EDGE,{"derivedFrom":[makeQuery(id+"F5.opExtrude","SWEPT_FACE",FACE,{"disambiguationData":[OSD([sQuery(id+"F4.wireOp",EDGE,"E5")])]}),makeQuery(id+"F11.opExtrude","SWEPT_FACE",FACE,{"disambiguationData":[OSD([sQuery(id+"F10.wireOp",EDGE,"E11.1.0")])]})]});
            var Q54;
            Q54=makeQuery(id+"F14.opBoolean","INTERSECT",EDGE,{"derivedFrom":[makeQuery(id+"F1.opExtrude","SWEPT_FACE",FACE,{"disambiguationData":[OSD([sQuery(id+"F0.wireOp",EDGE,"E1")])]}),makeQuery(id+"F9.opExtrude","SWEPT_FACE",FACE,{"disambiguationData":[OSD([sQuery(id+"F8.wireOp",EDGE,"E9.1.1")])]})]});
            var Q55;
            Q55=makeQuery(id+"F14.opBoolean","INTERSECT",EDGE,{"derivedFrom":[makeQuery(id+"F5.opExtrude","SWEPT_FACE",FACE,{"disambiguationData":[OSD([sQuery(id+"F4.wireOp",EDGE,"E5")])]}),makeQuery(id+"F11.opExtrude","SWEPT_FACE",FACE,{"disambiguationData":[OSD([sQuery(id+"F10.wireOp",EDGE,"E11.1.1")])]})]});
            var Q56;
            Q56=makeQuery(id+"F14.opBoolean","INTERSECT",EDGE,{"derivedFrom":[makeQuery(id+"F1.opExtrude","SWEPT_FACE",FACE,{"disambiguationData":[OSD([sQuery(id+"F0.wireOp",EDGE,"E1")])]}),makeQuery(id+"F9.opExtrude","SWEPT_FACE",FACE,{"disambiguationData":[OSD([sQuery(id+"F8.wireOp",EDGE,"E9.2.3")])]})]});
            var Q57;
            Q57=makeQuery(id+"F14.opBoolean","INTERSECT",EDGE,{"derivedFrom":[makeQuery(id+"F5.opExtrude","SWEPT_FACE",FACE,{"disambiguationData":[OSD([sQuery(id+"F4.wireOp",EDGE,"E5")])]}),makeQuery(id+"F11.opExtrude","SWEPT_FACE",FACE,{"disambiguationData":[OSD([sQuery(id+"F10.wireOp",EDGE,"E11.2.0")])]})]});
            var Q58;
            Q58=makeQuery(id+"F14.opBoolean","INTERSECT",EDGE,{"derivedFrom":[makeQuery(id+"F1.opExtrude","SWEPT_FACE",FACE,{"disambiguationData":[OSD([sQuery(id+"F0.wireOp",EDGE,"E1")])]}),makeQuery(id+"F9.opExtrude","SWEPT_FACE",FACE,{"disambiguationData":[OSD([sQuery(id+"F8.wireOp",EDGE,"E9.2.1")])]})]});
            var Q59;
            Q59=makeQuery(id+"F14.opBoolean","INTERSECT",EDGE,{"derivedFrom":[makeQuery(id+"F5.opExtrude","SWEPT_FACE",FACE,{"disambiguationData":[OSD([sQuery(id+"F4.wireOp",EDGE,"E5")])]}),makeQuery(id+"F11.opExtrude","SWEPT_FACE",FACE,{"disambiguationData":[OSD([sQuery(id+"F10.wireOp",EDGE,"E11.2.1")])]})]});
            fillet(context, id + "F17", {"entities" : qUnion([Q0, Q1, Q2, Q3, Q4, Q5, Q6, Q7, Q8, Q9, Q10, Q11, Q12, Q13, Q14, Q15, Q16, Q17, Q18, Q19, Q20, Q21, Q22, Q23, Q24, Q25, Q26, Q27, Q28, Q29, Q30, Q31, Q32, Q33, Q34, Q35, Q36, Q37, Q38, Q39, Q40, Q41, Q42, Q43, Q44, Q45, Q46, Q47, Q48, Q49, Q50, Q51, Q52, Q53, Q54, Q55, Q56, Q57, Q58, Q59]), "radius" : 5 * mm, "tangentPropagation" : true, "allowEdgeOverflow" : false});
        }
    });
